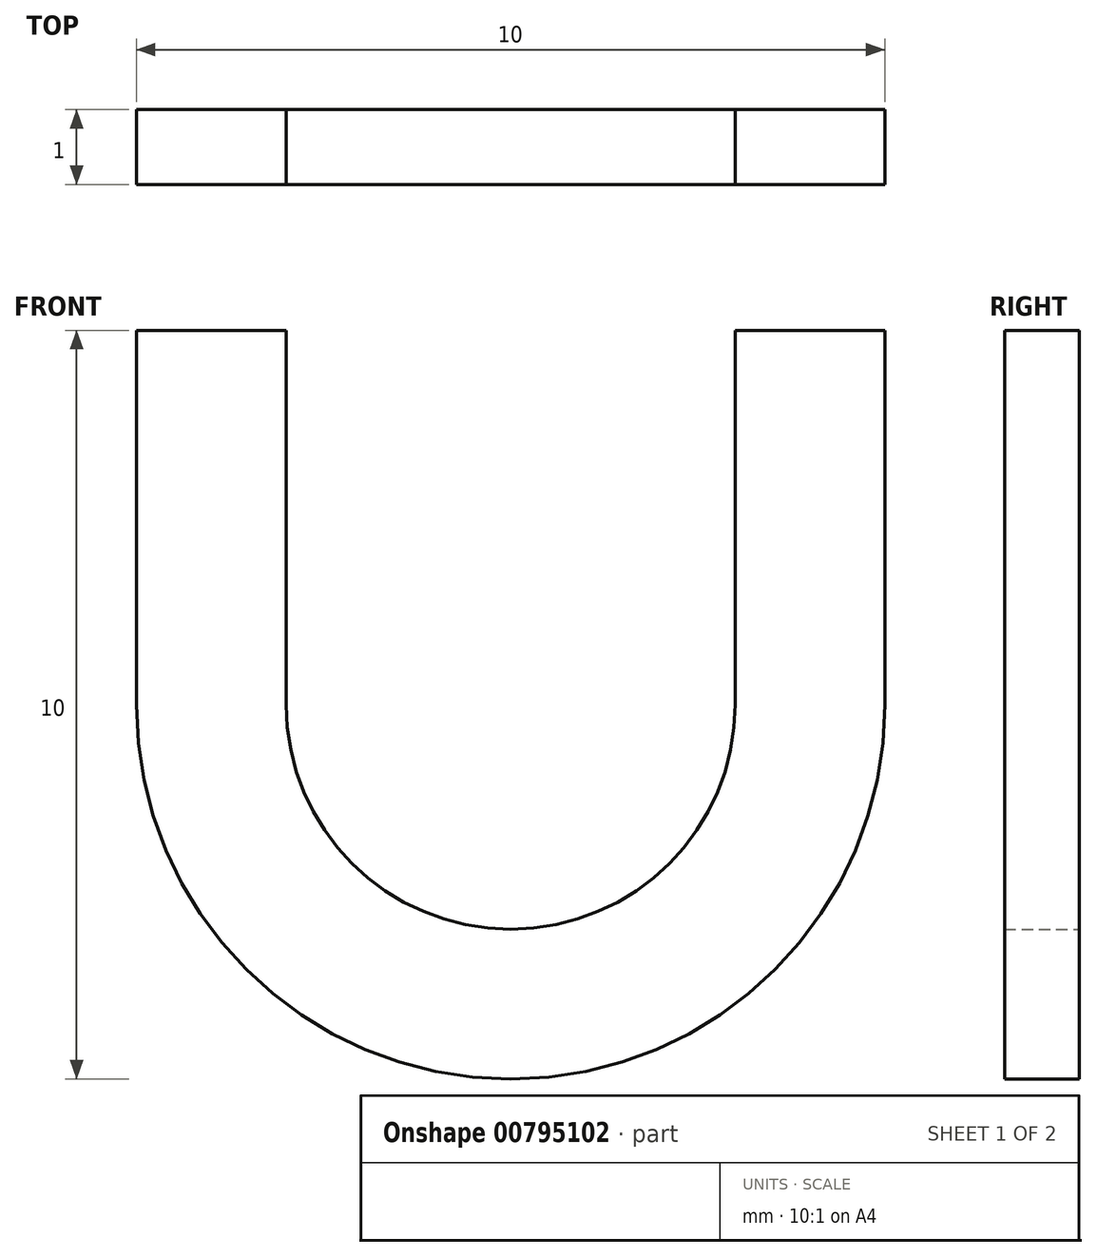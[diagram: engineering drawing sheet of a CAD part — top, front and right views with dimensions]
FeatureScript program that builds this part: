
annotation { "Feature Type Name" : "Feature", "Feature Type Description" : "" }
export const myFeature = defineFeature(function(context is Context, id is Id, definition is map)
    precondition{}
    {
        {
            var Q0;
            Q0=qCreatedBy(makeId("Front.planeOp"),FACE);
            var sketch = newSketch(context, id + "F0", { "sketchPlane" : qUnion([Q0])});
            skArc(sketch, "E0", {"start": v(-5, 0) * mm, "mid": v(0, -5) * mm, "end": v(5, 0) * mm});
            skArc(sketch, "E1", {"start": v(-3, 0) * mm, "mid": v(0, -3) * mm, "end": v(3, 0) * mm});
            skLineSegment(sketch, "E2", {"start": v(-5, 0) * mm, "end": v(-5, 5) * mm});
            skLineSegment(sketch, "E3", {"start": v(-5, 5) * mm, "end": v(-3, 5) * mm});
            skLineSegment(sketch, "E4", {"start": v(5, 0) * mm, "end": v(5, 5) * mm});
            skLineSegment(sketch, "E5", {"start": v(-3, 0) * mm, "end": v(-3, 5) * mm});
            skLineSegment(sketch, "E6", {"start": v(3, 0) * mm, "end": v(3, 5) * mm});
            skLineSegment(sketch, "E7.trimOffspring", {"start": v(3, 5) * mm, "end": v(5, 5) * mm});
            skSolve(sketch);
        }
        {
            var Q0;
            Q0 = qSketchRegion(id + "F0", true);
            extrude(context, id + "F1", {"entities" : qUnion([Q0]), "depth" : 1 * mm, "offsetDistance" : 25 * mm});
        }
    });
